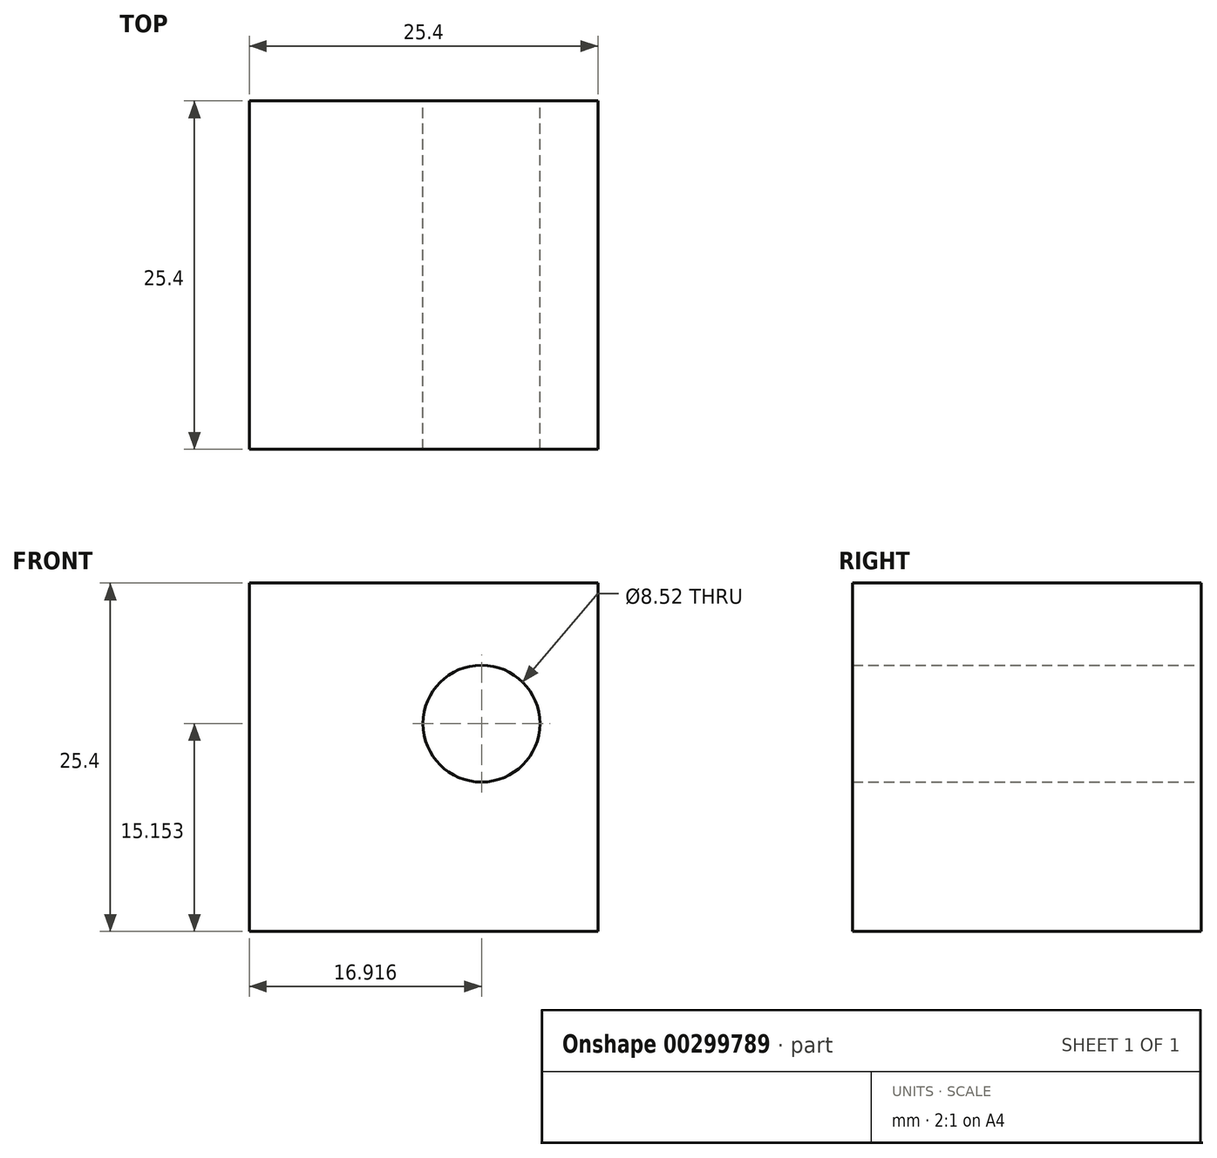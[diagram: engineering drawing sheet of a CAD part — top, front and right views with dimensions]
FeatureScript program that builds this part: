
annotation { "Feature Type Name" : "Feature", "Feature Type Description" : "" }
export const myFeature = defineFeature(function(context is Context, id is Id, definition is map)
    precondition{}
    {
        {
            var Q0;
            Q0=qCreatedBy(makeId("Front.planeOp"),FACE);
            var sketch = newSketch(context, id + "F0", { "sketchPlane" : qUnion([Q0])});
            skLineSegment(sketch, "E0", {"start": v(0, 25.4) * mm, "end": v(-25.4, 25.4) * mm});
            skLineSegment(sketch, "E1", {"start": v(-25.4, 25.4) * mm, "end": v(-25.4, 0) * mm});
            skLineSegment(sketch, "E2", {"start": v(-25.4, 0) * mm, "end": v(0, 0) * mm});
            skLineSegment(sketch, "E3", {"start": v(0, 0) * mm, "end": v(0, 25.4) * mm});
            skSolve(sketch);
        }
        {
            var Q0;
            Q0=makeQuery(id+"F0.imprint","IMPRINT",FACE,{"disambiguationData":[TD([[makeQuery(id+"F0.imprint","IMPRINT",EDGE,{"derivedFrom":sQuery(id+"F0.wireOp",EDGE,"E0")}),1.0]])]});
            var sketch = newSketch(context, id + "F1", { "sketchPlane" : qUnion([Q0])});
            skCircle(sketch, "E4", {"center": v(-11.76, 12.69) * mm, "radius": 7.93 * mm});
            skSolve(sketch);
        }
        {
            var Q0;
            Q0=makeQuery(id+"F0.imprint","IMPRINT",FACE,{"disambiguationData":[TD([[makeQuery(id+"F0.imprint","IMPRINT",EDGE,{"derivedFrom":sQuery(id+"F0.wireOp",EDGE,"E0")}),1.0]])]});
            extrude(context, id + "F2", {"entities" : qUnion([Q0]), "depth" : 25.4 * mm});
        }
        {
            var Q0;
            Q0=makeQuery(id+"F1.imprint","IMPRINT",FACE,{"disambiguationData":[TD([[makeQuery(id+"F1.imprint","IMPRINT",EDGE,{"derivedFrom":sQuery(id+"F1.wireOp",EDGE,"E4")}),1.0]])]});
            var sketch = newSketch(context, id + "F3", { "sketchPlane" : qUnion([Q0])});
            skFitSpline(sketch, "E5", {"points": [v(-22.66, 41.48) * mm, v(-51.42, 80.05) * mm, v(-50.88, 65.7) * mm, v(-50.39, 56.05) * mm, v(-36.53, 48.76) * mm, v(-17.95, 24.35) * mm, v(-22.66, 41.48) * mm]});
            skFitSpline(sketch, "E6", {"points": [v(-36.53, 57.4) * mm, v(-36.53, 55.55) * mm, v(-22.66, 39.74) * mm, v(-36.53, 41.48) * mm, v(-60.54, 72.71) * mm, v(-36.53, 57.4) * mm]});
            skSolve(sketch);
        }
        {
            var Q0;
            {var subQ0=sQuery(id+"F3.wireOp",EDGE,"E6");var subQ1=sQuery(id+"F3.wireOp",EDGE,"E5");var subQ2=makeQuery(id+"F3.imprint","INTERSECT",VERTEX,{"disambiguationData":[OD(0.0)],"derivedFrom":[subQ1,subQ0]});Q0=makeQuery(id+"F3.imprint","IMPRINT",FACE,{"disambiguationData":[TD([[makeQuery(id+"F3.imprint","IMPRINT",EDGE,{"disambiguationData":[TD([[subQ2,-1.0]])],"derivedFrom":subQ1}),1.0]])]});}
            extrude(context, id + "F4", {"entities" : qUnion([Q0]), "operationType" : NewBodyOperationType.REMOVE, "depth" : 23.37 * mm});
        }
        {
            var Q0;
            Q0=qCreatedBy(makeId("Front.planeOp"),FACE);
            var sketch = newSketch(context, id + "F5", { "sketchPlane" : qUnion([Q0])});
            skCircle(sketch, "E7", {"center": v(-8.48, 15.15) * mm, "radius": 4.26 * mm});
            skSolve(sketch);
        }
        {
            var Q0;
            Q0 = qSketchRegion(id + "F5", true);
            extrude(context, id + "F6", {"entities" : qUnion([Q0]), "operationType" : NewBodyOperationType.REMOVE, "depth" : 38.86 * mm});
        }
    });
